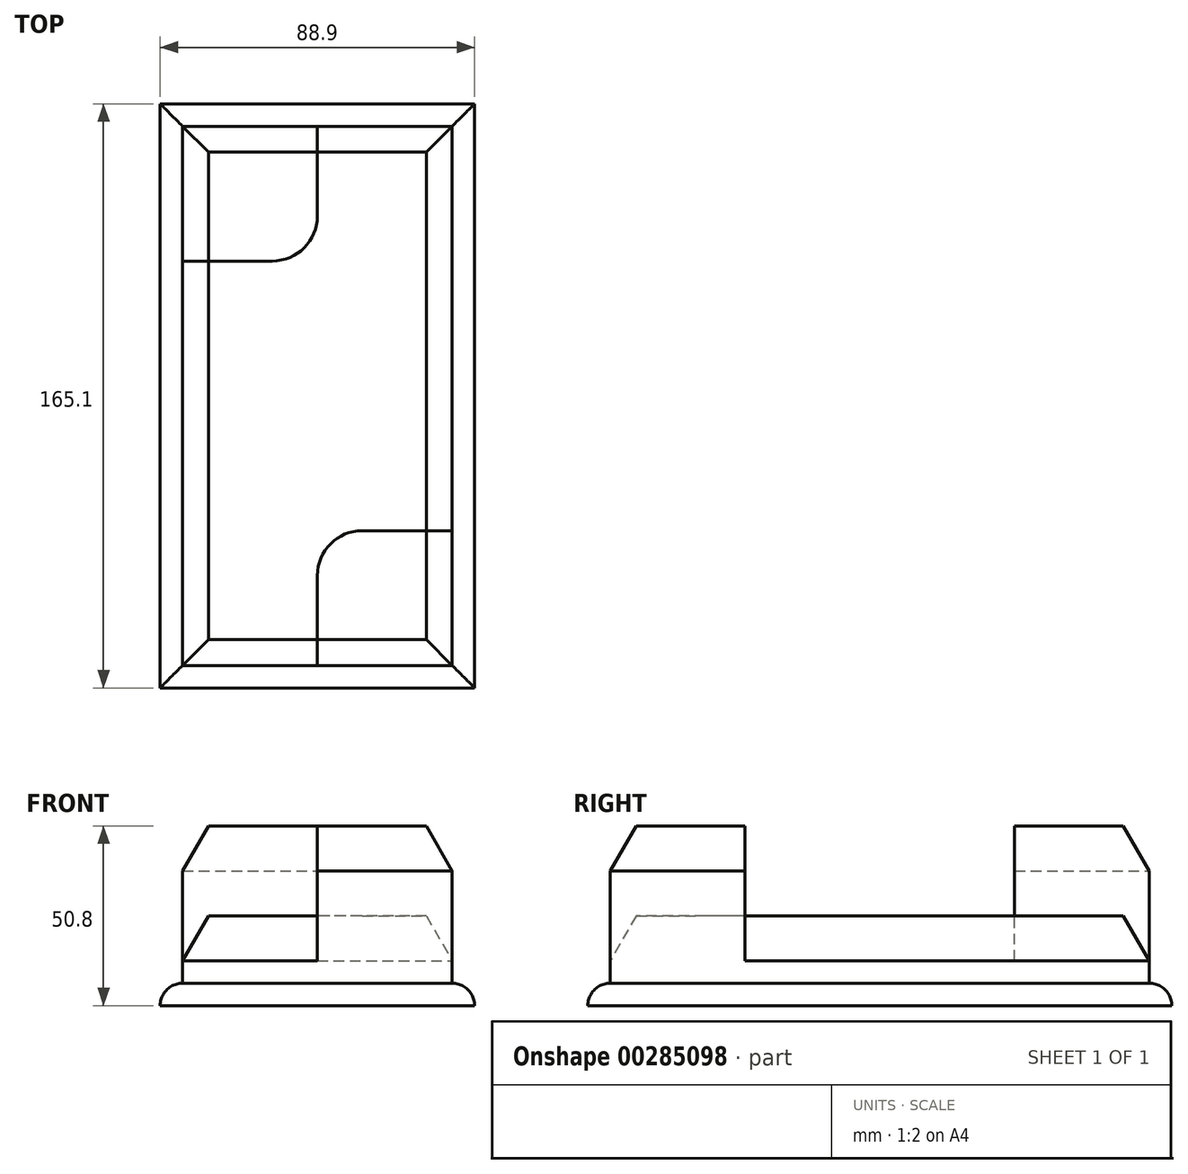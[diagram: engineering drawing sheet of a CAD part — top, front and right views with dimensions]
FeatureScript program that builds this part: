
annotation { "Feature Type Name" : "Feature", "Feature Type Description" : "" }
export const myFeature = defineFeature(function(context is Context, id is Id, definition is map)
    precondition{}
    {
        {
            var Q0;
            Q0=qCreatedBy(makeId("Top.planeOp"),FACE);
            var sketch = newSketch(context, id + "F0", { "sketchPlane" : qUnion([Q0])});
            skLineSegment(sketch, "E0.bottom", {"start": v(-76.2, 152.4) * mm, "end": v(0, 152.4) * mm});
            skLineSegment(sketch, "E0.top", {"start": v(-76.2, 0) * mm, "end": v(0, 0) * mm});
            skLineSegment(sketch, "E0.left", {"start": v(-76.2, 152.4) * mm, "end": v(-76.2, 0) * mm});
            skLineSegment(sketch, "E0.right", {"start": v(0, 152.4) * mm, "end": v(0, 0) * mm});
            skLineSegment(sketch, "E1.0", {"start": v(-82.55, 158.75) * mm, "end": v(6.35, 158.75) * mm});
            skLineSegment(sketch, "E1.1", {"start": v(-82.55, 158.75) * mm, "end": v(-82.55, -6.35) * mm});
            skLineSegment(sketch, "E1.2", {"start": v(-82.55, -6.35) * mm, "end": v(6.35, -6.35) * mm});
            skLineSegment(sketch, "E1.3", {"start": v(6.35, 158.75) * mm, "end": v(6.35, -6.35) * mm});
            skLineSegment(sketch, "E2", {"start": v(-38.1, 152.4) * mm, "end": v(-38.1, 127) * mm});
            skPoint(sketch, "E2.endSnap0", {"position": v(-38.1, 152.4) * mm});
            skLineSegment(sketch, "E3", {"start": v(-50.8, 114.3) * mm, "end": v(-76.2, 114.3) * mm});
            skLineSegment(sketch, "E4", {"start": v(-38.1, 0) * mm, "end": v(-38.1, 25.4) * mm});
            skLineSegment(sketch, "E5", {"start": v(-25.4, 38.1) * mm, "end": v(0, 38.1) * mm});
            skPoint(sketch, "E6.visualSharp", {"position": v(-38.1, 114.3) * mm});
            skArc(sketch, "E6.filletArc", {"start": v(-50.8, 114.3) * mm, "mid": v(-41.82, 118.02) * mm, "end": v(-38.1, 127) * mm});
            skPoint(sketch, "E7.visualSharp", {"position": v(-38.1, 38.1) * mm});
            skArc(sketch, "E7.filletArc", {"start": v(-25.4, 38.1) * mm, "mid": v(-34.38, 34.38) * mm, "end": v(-38.1, 25.4) * mm});
            skSolve(sketch);
        }
        {
            var Q0;
            Q0=makeQuery(id+"F0.imprint","IMPRINT",FACE,{"disambiguationData":[TD([[makeQuery(id+"F0.imprint","IMPRINT",EDGE,{"derivedFrom":sQuery(id+"F0.wireOp",EDGE,"E1.0")}),-1.0]])]});
            extrude(context, id + "F1", {"entities" : qUnion([Q0]), "depth" : 6.35 * mm});
        }
        {
            var Q0;
            {var subQ9=sQuery(id+"F0.wireOp",EDGE,"E2");Q0=makeQuery(id+"F0.imprint","IMPRINT",FACE,{"disambiguationData":[TD([[makeQuery(id+"F0.imprint","IMPRINT",EDGE,{"derivedFrom":subQ9}),1.0]])]});}
            extrude(context, id + "F2", {"entities" : qUnion([Q0]), "operationType" : NewBodyOperationType.ADD, "depth" : 25.4 * mm});
        }
        {
            var Q0;
            {var subQ1=sQuery(id+"F0.wireOp",EDGE,"E2");Q0=makeQuery(id+"F0.imprint","IMPRINT",FACE,{"disambiguationData":[TD([[makeQuery(id+"F0.imprint","IMPRINT",EDGE,{"derivedFrom":subQ1}),-1.0]])]});}
            var Q1;
            {var subQ1=sQuery(id+"F0.wireOp",EDGE,"E4");Q1=makeQuery(id+"F0.imprint","IMPRINT",FACE,{"disambiguationData":[TD([[makeQuery(id+"F0.imprint","IMPRINT",EDGE,{"derivedFrom":subQ1}),-1.0]])]});}
            extrude(context, id + "F3", {"entities" : qUnion([Q0, Q1]), "operationType" : NewBodyOperationType.ADD, "depth" : 50.8 * mm});
        }
        {
            var Q0;
            Q0=makeQuery(id+"F1.opExtrude","CAP_EDGE",EDGE,{"disambiguationData":[OSD([sQuery(id+"F0.wireOp",EDGE,"E1.3")])],"isStart":false});
            var Q1;
            Q1=makeQuery(id+"F1.opExtrude","CAP_EDGE",EDGE,{"disambiguationData":[OSD([sQuery(id+"F0.wireOp",EDGE,"E1.0")])],"isStart":false});
            var Q2;
            Q2=makeQuery(id+"F1.opExtrude","CAP_EDGE",EDGE,{"disambiguationData":[OSD([sQuery(id+"F0.wireOp",EDGE,"E1.1")])],"isStart":false});
            var Q3;
            Q3=makeQuery(id+"F1.opExtrude","CAP_EDGE",EDGE,{"disambiguationData":[OSD([sQuery(id+"F0.wireOp",EDGE,"E1.2")])],"isStart":false});
            fillet(context, id + "F4", {"entities" : qUnion([Q0, Q1, Q2, Q3]), "radius" : 6.35 * mm, "tangentPropagation" : true, "allowEdgeOverflow" : false});
        }
        {
            var Q0;
            Q0=makeQuery(id+"F2.opExtrude","CAP_EDGE",EDGE,{"disambiguationData":[OSD([sQuery(id+"F0.wireOp",EDGE,"E0.right")])],"isStart":false});
            var Q1;
            Q1=makeQuery(id+"F2.opExtrude","CAP_EDGE",EDGE,{"disambiguationData":[OSD([sQuery(id+"F0.wireOp",EDGE,"E0.top")])],"isStart":false});
            var Q2;
            Q2=makeQuery(id+"F2.opExtrude","CAP_EDGE",EDGE,{"disambiguationData":[OSD([sQuery(id+"F0.wireOp",EDGE,"E0.left")])],"isStart":false});
            var Q3;
            Q3=makeQuery(id+"F2.opExtrude","CAP_EDGE",EDGE,{"disambiguationData":[OSD([sQuery(id+"F0.wireOp",EDGE,"E0.bottom")])],"isStart":false});
            chamfer(context, id + "F5", {"entities" : qUnion([Q0, Q1, Q2, Q3]), "chamferType" : ChamferType.OFFSET_ANGLE, "width" : 12.7 * mm, "oppositeDirection" : false, "angle" : 30 * degree, "tangentPropagation" : true});
        }
        {
            var Q0;
            Q0=makeQuery(id+"F3.opExtrude","CAP_EDGE",EDGE,{"disambiguationData":[OSD([sQuery(id+"F0.wireOp",EDGE,"E0.bottom")])],"isStart":false});
            var Q1;
            Q1=makeQuery(id+"F3.opExtrude","CAP_EDGE",EDGE,{"disambiguationData":[OSD([sQuery(id+"F0.wireOp",EDGE,"E0.left")])],"isStart":false});
            chamfer(context, id + "F6", {"entities" : qUnion([Q0, Q1]), "chamferType" : ChamferType.OFFSET_ANGLE, "width" : 12.7 * mm, "oppositeDirection" : false, "angle" : 30 * degree, "tangentPropagation" : true});
        }
        {
            var Q0;
            Q0=makeQuery(id+"F3.opExtrude","CAP_EDGE",EDGE,{"disambiguationData":[OSD([sQuery(id+"F0.wireOp",EDGE,"E0.right")])],"isStart":false});
            var Q1;
            Q1=makeQuery(id+"F3.opExtrude","CAP_EDGE",EDGE,{"disambiguationData":[OSD([sQuery(id+"F0.wireOp",EDGE,"E0.top")])],"isStart":false});
            chamfer(context, id + "F7", {"entities" : qUnion([Q0, Q1]), "chamferType" : ChamferType.OFFSET_ANGLE, "width" : 12.7 * mm, "oppositeDirection" : false, "angle" : 30 * degree, "tangentPropagation" : true});
        }
    });
